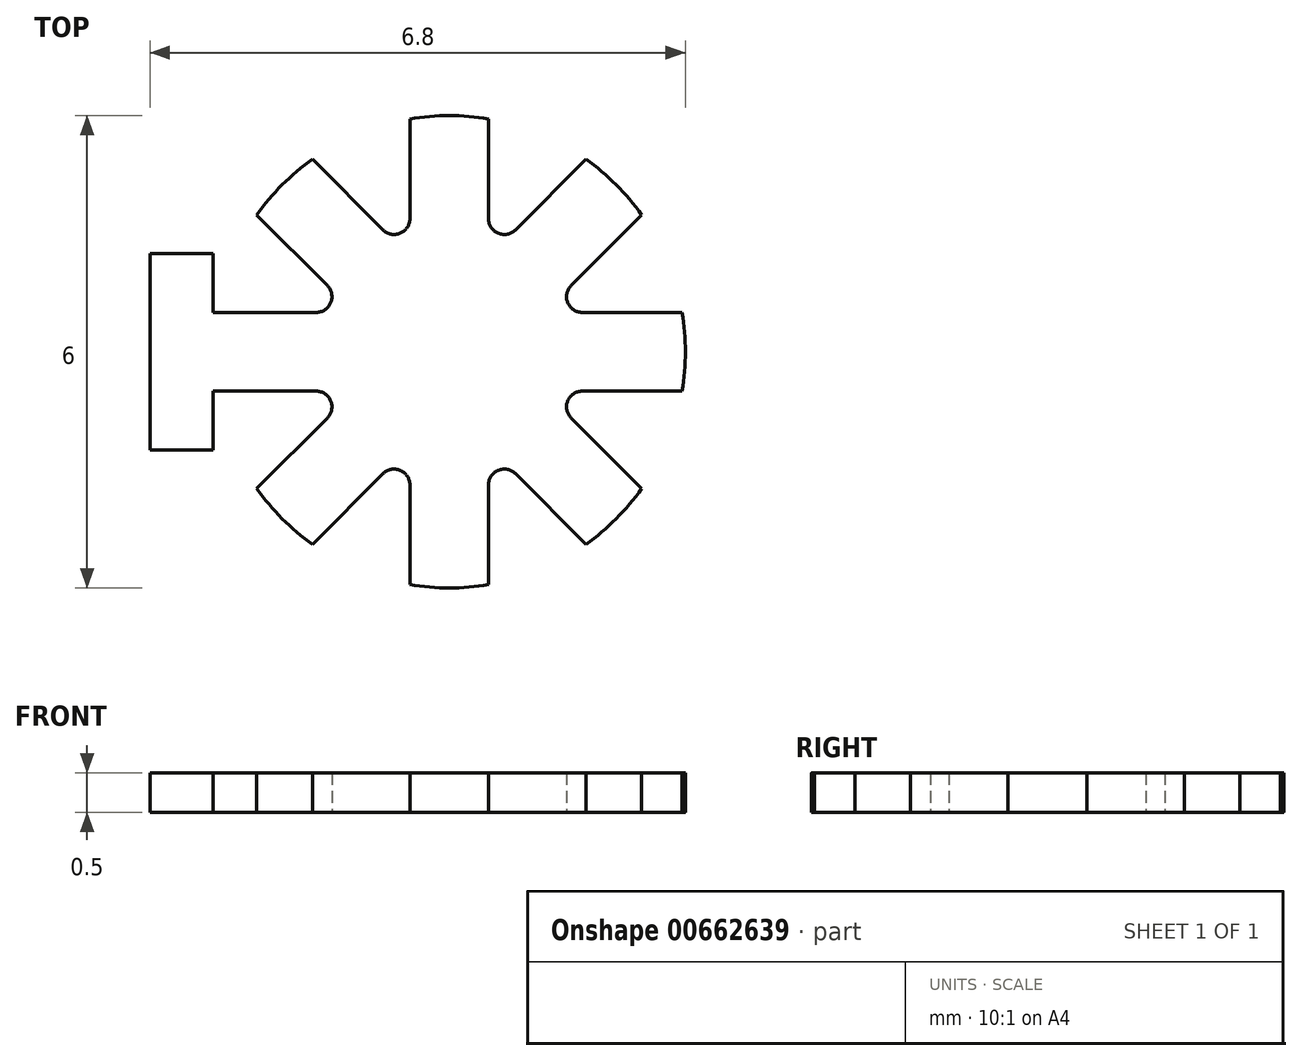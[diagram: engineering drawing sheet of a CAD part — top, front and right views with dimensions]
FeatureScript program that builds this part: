
annotation { "Feature Type Name" : "Feature", "Feature Type Description" : "" }
export const myFeature = defineFeature(function(context is Context, id is Id, definition is map)
    precondition{}
    {
        {
            var Q0;
            Q0=qCreatedBy(makeId("Top.planeOp"),FACE);
            var sketch = newSketch(context, id + "F0", { "sketchPlane" : qUnion([Q0])});
            skArc(sketch, "E0", {"start": v(0.5, 2.96) * mm, "mid": v(0, 3) * mm, "end": v(-0.5, 2.96) * mm});
            skLineSegment(sketch, "E1", {"start": v(-0.5, 2.96) * mm, "end": v(-0.5, 1.69) * mm});
            skLineSegment(sketch, "E2", {"start": v(0.5, 2.96) * mm, "end": v(0.5, 1.69) * mm});
            skArc(sketch, "E3.1.0", {"start": v(-1.74, 2.45) * mm, "mid": v(-2.12, 2.12) * mm, "end": v(-2.45, 1.74) * mm});
            skLineSegment(sketch, "E3.1.1", {"start": v(-2.45, 1.74) * mm, "end": v(-1.55, 0.84) * mm});
            skLineSegment(sketch, "E3.1.2", {"start": v(-1.74, 2.45) * mm, "end": v(-0.84, 1.55) * mm});
            skLineSegment(sketch, "E3.2.1", {"start": v(-3, -0.5) * mm, "end": v(-1.69, -0.5) * mm});
            skLineSegment(sketch, "E3.2.2", {"start": v(-3, 0.5) * mm, "end": v(-1.69, 0.5) * mm});
            skArc(sketch, "E3.3.0", {"start": v(-2.45, -1.74) * mm, "mid": v(-2.12, -2.12) * mm, "end": v(-1.74, -2.45) * mm});
            skLineSegment(sketch, "E3.3.1", {"start": v(-1.74, -2.45) * mm, "end": v(-0.84, -1.55) * mm});
            skLineSegment(sketch, "E3.3.2", {"start": v(-2.45, -1.74) * mm, "end": v(-1.55, -0.84) * mm});
            skArc(sketch, "E3.4.0", {"start": v(-0.5, -2.96) * mm, "mid": v(0, -3) * mm, "end": v(0.5, -2.96) * mm});
            skLineSegment(sketch, "E3.4.1", {"start": v(0.5, -2.96) * mm, "end": v(0.5, -1.69) * mm});
            skLineSegment(sketch, "E3.4.2", {"start": v(-0.5, -2.96) * mm, "end": v(-0.5, -1.69) * mm});
            skArc(sketch, "E3.5.0", {"start": v(1.74, -2.45) * mm, "mid": v(2.12, -2.12) * mm, "end": v(2.45, -1.74) * mm});
            skLineSegment(sketch, "E3.5.1", {"start": v(2.45, -1.74) * mm, "end": v(1.55, -0.84) * mm});
            skLineSegment(sketch, "E3.5.2", {"start": v(1.74, -2.45) * mm, "end": v(0.84, -1.55) * mm});
            skArc(sketch, "E3.6.0", {"start": v(2.96, -0.5) * mm, "mid": v(3, 0) * mm, "end": v(2.96, 0.5) * mm});
            skLineSegment(sketch, "E3.6.1", {"start": v(2.96, 0.5) * mm, "end": v(1.69, 0.5) * mm});
            skLineSegment(sketch, "E3.6.2", {"start": v(2.96, -0.5) * mm, "end": v(1.69, -0.5) * mm});
            skArc(sketch, "E3.7.0", {"start": v(2.45, 1.74) * mm, "mid": v(2.12, 2.12) * mm, "end": v(1.74, 2.45) * mm});
            skLineSegment(sketch, "E3.7.1", {"start": v(1.74, 2.45) * mm, "end": v(0.84, 1.55) * mm});
            skLineSegment(sketch, "E3.7.2", {"start": v(2.45, 1.74) * mm, "end": v(1.55, 0.84) * mm});
            skCircle(sketch, "E4", {"center": v(0, 0) * mm, "radius": 1.5 * mm, "construction": true});
            skPoint(sketch, "E5.newPointA", {"position": v(-0.5, 1.55) * mm});
            skPoint(sketch, "E5.newPointB", {"position": v(-0.74, 1.45) * mm});
            skArc(sketch, "E5.filletArc", {"start": v(-0.84, 1.55) * mm, "mid": v(-0.62, 1.5) * mm, "end": v(-0.5, 1.69) * mm});
            skPoint(sketch, "E6.newPointA", {"position": v(-1.45, 0.74) * mm});
            skPoint(sketch, "E6.newPointB", {"position": v(-1.55, 0.5) * mm});
            skArc(sketch, "E6.filletArc", {"start": v(-1.69, 0.5) * mm, "mid": v(-1.5, 0.62) * mm, "end": v(-1.55, 0.84) * mm});
            skPoint(sketch, "E7.newPointA", {"position": v(-1.55, -0.5) * mm});
            skPoint(sketch, "E7.newPointB", {"position": v(-1.45, -0.74) * mm});
            skArc(sketch, "E7.filletArc", {"start": v(-1.55, -0.84) * mm, "mid": v(-1.5, -0.62) * mm, "end": v(-1.69, -0.5) * mm});
            skPoint(sketch, "E8.newPointA", {"position": v(0.5, 1.55) * mm});
            skPoint(sketch, "E8.newPointB", {"position": v(0.74, 1.45) * mm});
            skArc(sketch, "E8.filletArc", {"start": v(0.5, 1.69) * mm, "mid": v(0.62, 1.5) * mm, "end": v(0.84, 1.55) * mm});
            skPoint(sketch, "E9.newPointA", {"position": v(1.45, 0.74) * mm});
            skPoint(sketch, "E9.newPointB", {"position": v(1.55, 0.5) * mm});
            skArc(sketch, "E9.filletArc", {"start": v(1.55, 0.84) * mm, "mid": v(1.5, 0.62) * mm, "end": v(1.69, 0.5) * mm});
            skPoint(sketch, "E10.newPointA", {"position": v(1.55, -0.5) * mm});
            skPoint(sketch, "E10.newPointB", {"position": v(1.45, -0.74) * mm});
            skArc(sketch, "E10.filletArc", {"start": v(1.69, -0.5) * mm, "mid": v(1.5, -0.62) * mm, "end": v(1.55, -0.84) * mm});
            skPoint(sketch, "E11.newPointA", {"position": v(0.74, -1.45) * mm});
            skPoint(sketch, "E11.newPointB", {"position": v(0.5, -1.55) * mm});
            skArc(sketch, "E11.filletArc", {"start": v(0.84, -1.55) * mm, "mid": v(0.62, -1.5) * mm, "end": v(0.5, -1.69) * mm});
            skPoint(sketch, "E12.newPointA", {"position": v(-0.74, -1.45) * mm});
            skPoint(sketch, "E12.newPointB", {"position": v(-0.5, -1.55) * mm});
            skArc(sketch, "E12.filletArc", {"start": v(-0.5, -1.69) * mm, "mid": v(-0.62, -1.5) * mm, "end": v(-0.84, -1.55) * mm});
            skLineSegment(sketch, "E13", {"start": v(-3.8, 1.25) * mm, "end": v(-3.8, -1.25) * mm});
            skLineSegment(sketch, "E14", {"start": v(-3.8, -1.25) * mm, "end": v(-3, -1.25) * mm});
            skLineSegment(sketch, "E15", {"start": v(-3, -1.25) * mm, "end": v(-3, -0.5) * mm});
            skLineSegment(sketch, "E16", {"start": v(-3.8, 1.25) * mm, "end": v(-3, 1.25) * mm});
            skPoint(sketch, "E17.orphan", {"position": v(-2.96, 0.5) * mm});
            skPoint(sketch, "E18.orphan", {"position": v(-2.96, -0.5) * mm});
            skLineSegment(sketch, "E19.trimOffspring", {"start": v(-3, 0.5) * mm, "end": v(-3, 1.25) * mm});
            skSolve(sketch);
        }
        {
            var Q0;
            Q0=makeQuery(id+"F0.imprint","IMPRINT",FACE,{"disambiguationData":[TD([[makeQuery(id+"F0.imprint","IMPRINT",EDGE,{"derivedFrom":sQuery(id+"F0.wireOp",EDGE,"E0")}),1.0]])]});
            extrude(context, id + "F1", {"entities" : qUnion([Q0]), "depth" : .5 * mm, "offsetDistance" : 25 * mm});
        }
    });
